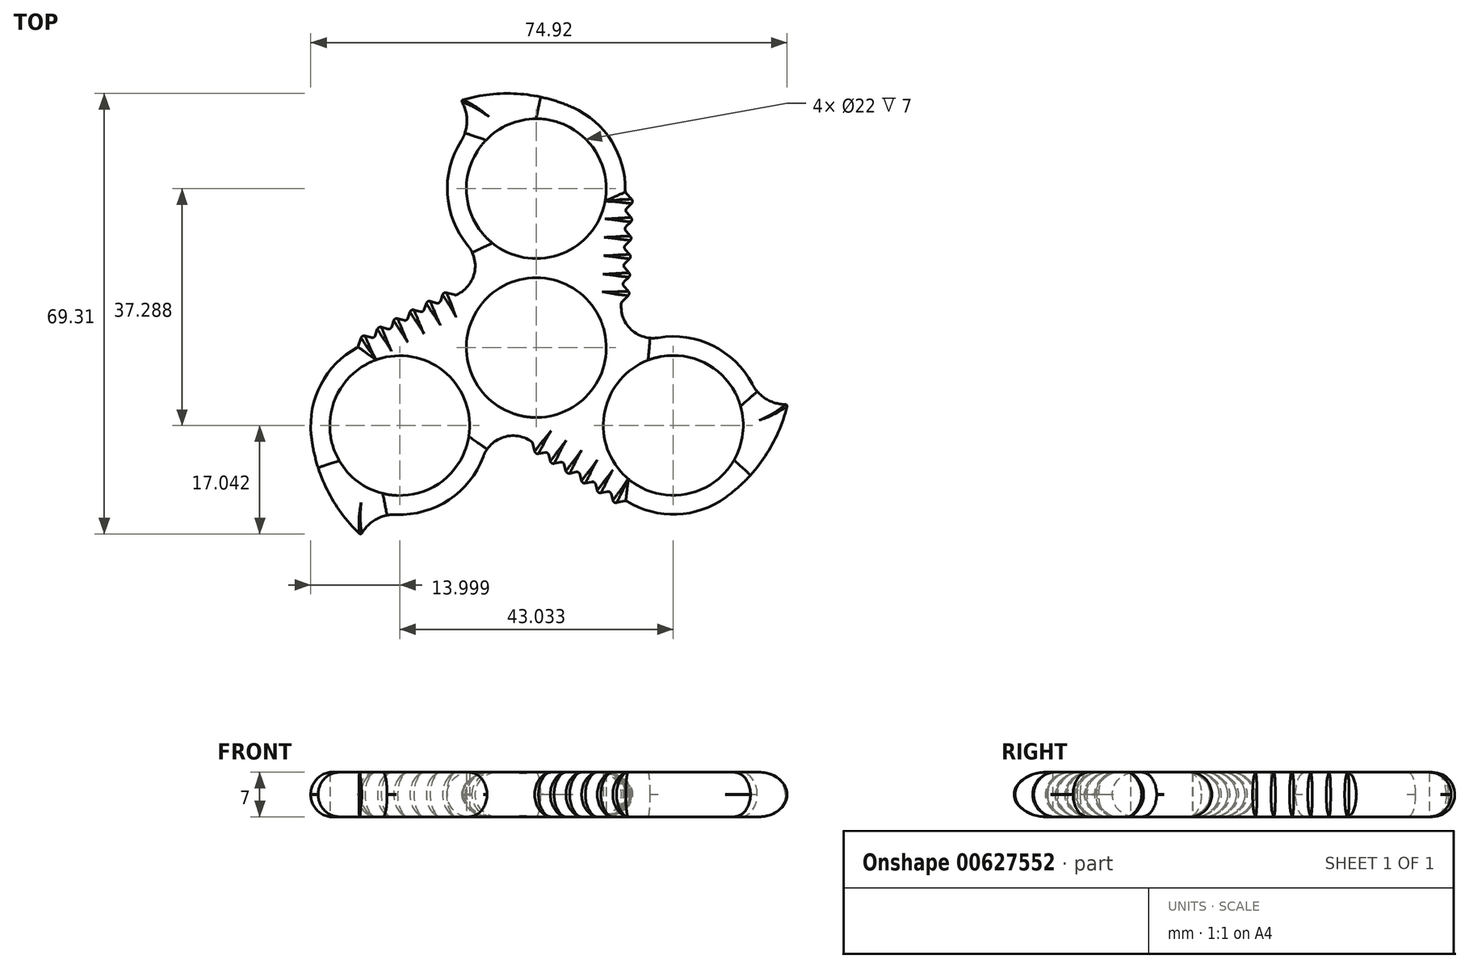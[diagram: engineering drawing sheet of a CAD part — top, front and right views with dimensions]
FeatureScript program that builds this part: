
annotation { "Feature Type Name" : "Feature", "Feature Type Description" : "" }
export const myFeature = defineFeature(function(context is Context, id is Id, definition is map)
    precondition{}
    {
        {
            var Q0;
            Q0=qCreatedBy(makeId("Top.planeOp"),FACE);
            var sketch = newSketch(context, id + "F0", { "sketchPlane" : qUnion([Q0])});
            skCircle(sketch, "E0", {"center": v(0, 0) * mm, "radius": 39 * mm, "construction": true});
            skCircle(sketch, "E1", {"center": v(0, 0) * mm, "radius": 25 * mm, "construction": true});
            skCircle(sketch, "E2", {"center": v(0, 0) * mm, "radius": 11 * mm});
            skCircle(sketch, "E3", {"center": v(0, 25) * mm, "radius": 11 * mm});
            skPoint(sketch, "E4.center", {"position": v(0.03, 0) * mm});
            skArc(sketch, "E5", {"start": v(14, 24.5) * mm, "mid": v(11.9, 32.39) * mm, "end": v(5.75, 37.77) * mm});
            skLineSegment(sketch, "E6", {"start": v(13.35, 6.66) * mm, "end": v(13.36, 7.1) * mm});
            skPoint(sketch, "E7.visualSharp", {"position": v(-4.7, 11.81) * mm});
            skArc(sketch, "E7.filletArc", {"start": v(-12.27, 8.44) * mm, "mid": v(-9.7, 11.89) * mm, "end": v(-10.77, 16.05) * mm});
            skPoint(sketch, "E8.visualSharp", {"position": v(13.05, -1.63) * mm});
            skArc(sketch, "E9", {"start": v(5.75, 37.77) * mm, "mid": v(-2.94, 39.93) * mm, "end": v(-11.83, 38.9) * mm});
            skArc(sketch, "E10", {"start": v(-11.83, 32.48) * mm, "mid": v(-10.9, 35.7) * mm, "end": v(-11.83, 38.9) * mm});
            skArc(sketch, "E11.trimOffspring", {"start": v(-11.83, 32.48) * mm, "mid": v(-13.97, 24.1) * mm, "end": v(-10.77, 16.05) * mm});
            skLineSegment(sketch, "E12", {"start": v(14, 24.5) * mm, "end": v(15.31, 23) * mm});
            skLineSegment(sketch, "E13", {"start": v(15.31, 23) * mm, "end": v(13.89, 21.6) * mm});
            skLineSegment(sketch, "E14.1.0.0", {"start": v(15.2, 20.1) * mm, "end": v(13.78, 18.7) * mm});
            skLineSegment(sketch, "E14.1.0.1", {"start": v(13.89, 21.6) * mm, "end": v(15.2, 20.1) * mm});
            skLineSegment(sketch, "E14.2.0.0", {"start": v(15.1, 17.2) * mm, "end": v(13.68, 15.8) * mm});
            skLineSegment(sketch, "E14.2.0.1", {"start": v(13.78, 18.7) * mm, "end": v(15.1, 17.2) * mm});
            skLineSegment(sketch, "E14.3.0.0", {"start": v(15, 14.3) * mm, "end": v(13.57, 12.9) * mm});
            skLineSegment(sketch, "E14.3.0.1", {"start": v(13.68, 15.8) * mm, "end": v(15, 14.3) * mm});
            skLineSegment(sketch, "E14.4.0.0", {"start": v(14.9, 11.4) * mm, "end": v(13.47, 10) * mm});
            skLineSegment(sketch, "E14.4.0.1", {"start": v(13.57, 12.9) * mm, "end": v(14.9, 11.4) * mm});
            skLineSegment(sketch, "E14.5.0.0", {"start": v(14.79, 8.5) * mm, "end": v(13.36, 7.1) * mm});
            skLineSegment(sketch, "E14.5.0.1", {"start": v(13.47, 10) * mm, "end": v(14.79, 8.5) * mm});
            skArc(sketch, "E15.1.0", {"start": v(-22.04, -26.28) * mm, "mid": v(-25.29, -27.08) * mm, "end": v(-27.6, -29.49) * mm});
            skArc(sketch, "E15.1.1", {"start": v(-1, -14.64) * mm, "mid": v(-5.27, -14.14) * mm, "end": v(-8.35, -17.14) * mm});
            skArc(sketch, "E15.1.2", {"start": v(-22.04, -26.28) * mm, "mid": v(-13.71, -23.93) * mm, "end": v(-8.35, -17.14) * mm});
            skArc(sketch, "E15.1.3", {"start": v(-35.41, -13.7) * mm, "mid": v(-32.94, -22.3) * mm, "end": v(-27.6, -29.49) * mm});
            skArc(sketch, "E15.1.4", {"start": v(-28.04, 0.08) * mm, "mid": v(-33.82, -5.68) * mm, "end": v(-35.41, -13.7) * mm});
            skCircle(sketch, "E15.1.5", {"center": v(-21.48, -12.29) * mm, "radius": 11 * mm});
            skLineSegment(sketch, "E15.1.6", {"start": v(-28.04, 0.08) * mm, "end": v(-27.4, 1.98) * mm});
            skLineSegment(sketch, "E15.1.7", {"start": v(-27.4, 1.98) * mm, "end": v(-25.47, 1.44) * mm});
            skLineSegment(sketch, "E15.1.8", {"start": v(-25.48, 1.44) * mm, "end": v(-24.84, 3.34) * mm});
            skLineSegment(sketch, "E15.1.9", {"start": v(-24.84, 3.34) * mm, "end": v(-22.91, 2.8) * mm});
            skLineSegment(sketch, "E15.1.10", {"start": v(-22.91, 2.8) * mm, "end": v(-22.28, 4.7) * mm});
            skLineSegment(sketch, "E15.1.11", {"start": v(-22.28, 4.7) * mm, "end": v(-20.35, 4.16) * mm});
            skLineSegment(sketch, "E15.1.12", {"start": v(-20.35, 4.16) * mm, "end": v(-19.71, 6.05) * mm});
            skLineSegment(sketch, "E15.1.13", {"start": v(-19.71, 6.05) * mm, "end": v(-17.79, 5.52) * mm});
            skLineSegment(sketch, "E15.1.14", {"start": v(-17.79, 5.51) * mm, "end": v(-17.15, 7.41) * mm});
            skLineSegment(sketch, "E15.1.15", {"start": v(-17.15, 7.41) * mm, "end": v(-15.23, 6.87) * mm});
            skLineSegment(sketch, "E15.1.16", {"start": v(-15.23, 6.87) * mm, "end": v(-14.59, 8.77) * mm});
            skLineSegment(sketch, "E15.1.17", {"start": v(-14.59, 8.77) * mm, "end": v(-12.66, 8.23) * mm});
            skLineSegment(sketch, "E15.1.18", {"start": v(-12.27, 8.44) * mm, "end": v(-12.66, 8.23) * mm});
            skArc(sketch, "E15.2.0", {"start": v(33.95, -5.74) * mm, "mid": v(36.26, -8.15) * mm, "end": v(39.5, -8.95) * mm});
            skArc(sketch, "E15.2.1", {"start": v(13.35, 6.66) * mm, "mid": v(15.05, 2.72) * mm, "end": v(19.19, 1.55) * mm});
            skArc(sketch, "E15.2.2", {"start": v(33.95, -5.74) * mm, "mid": v(27.75, 0.3) * mm, "end": v(19.19, 1.55) * mm});
            skArc(sketch, "E15.2.3", {"start": v(29.73, -23.6) * mm, "mid": v(35.95, -17.16) * mm, "end": v(39.5, -8.95) * mm});
            skArc(sketch, "E15.2.4", {"start": v(14.12, -24.11) * mm, "mid": v(22, -26.24) * mm, "end": v(29.73, -23.6) * mm});
            skCircle(sketch, "E15.2.5", {"center": v(21.55, -12.25) * mm, "radius": 11 * mm});
            skLineSegment(sketch, "E15.2.6", {"start": v(14.12, -24.11) * mm, "end": v(12.16, -24.5) * mm});
            skLineSegment(sketch, "E15.2.7", {"start": v(12.16, -24.5) * mm, "end": v(11.66, -22.57) * mm});
            skLineSegment(sketch, "E15.2.8", {"start": v(11.66, -22.57) * mm, "end": v(9.7, -22.97) * mm});
            skLineSegment(sketch, "E15.2.9", {"start": v(9.7, -22.97) * mm, "end": v(9.2, -21.03) * mm});
            skLineSegment(sketch, "E15.2.10", {"start": v(9.2, -21.03) * mm, "end": v(7.24, -21.43) * mm});
            skLineSegment(sketch, "E15.2.11", {"start": v(7.24, -21.43) * mm, "end": v(6.74, -19.5) * mm});
            skLineSegment(sketch, "E15.2.12", {"start": v(6.75, -19.5) * mm, "end": v(4.79, -19.89) * mm});
            skLineSegment(sketch, "E15.2.13", {"start": v(4.79, -19.89) * mm, "end": v(4.29, -17.95) * mm});
            skLineSegment(sketch, "E15.2.14", {"start": v(4.29, -17.95) * mm, "end": v(2.33, -18.35) * mm});
            skLineSegment(sketch, "E15.2.15", {"start": v(2.33, -18.35) * mm, "end": v(1.83, -16.41) * mm});
            skLineSegment(sketch, "E15.2.16", {"start": v(1.83, -16.41) * mm, "end": v(-0.13, -16.8) * mm});
            skLineSegment(sketch, "E15.2.17", {"start": v(-0.13, -16.8) * mm, "end": v(-0.63, -14.87) * mm});
            skLineSegment(sketch, "E15.2.18", {"start": v(-1, -14.64) * mm, "end": v(-0.63, -14.87) * mm});
            skPoint(sketch, "E15.center", {"position": v(0.02, 0.15) * mm});
            skLineSegment(sketch, "E16.trimOffspring", {"start": v(-25.47, 1.44) * mm, "end": v(-25.48, 1.44) * mm});
            skLineSegment(sketch, "E17.trimOffspring", {"start": v(-22.91, 2.8) * mm, "end": v(-22.91, 2.8) * mm});
            skLineSegment(sketch, "E18.trimOffspring", {"start": v(-20.35, 4.16) * mm, "end": v(-20.35, 4.16) * mm});
            skLineSegment(sketch, "E19.trimOffspring", {"start": v(-17.79, 5.52) * mm, "end": v(-17.79, 5.51) * mm});
            skLineSegment(sketch, "E20.trimOffspring", {"start": v(-15.23, 6.87) * mm, "end": v(-15.23, 6.87) * mm});
            skLineSegment(sketch, "E21.trimOffspring", {"start": v(1.83, -16.41) * mm, "end": v(1.83, -16.41) * mm});
            skLineSegment(sketch, "E22.trimOffspring", {"start": v(4.29, -17.95) * mm, "end": v(4.29, -17.95) * mm});
            skLineSegment(sketch, "E23.trimOffspring", {"start": v(6.74, -19.5) * mm, "end": v(6.75, -19.5) * mm});
            skLineSegment(sketch, "E24.trimOffspring", {"start": v(9.2, -21.03) * mm, "end": v(9.2, -21.03) * mm});
            skLineSegment(sketch, "E25.trimOffspring", {"start": v(11.26, -22.32) * mm, "end": v(11.66, -22.57) * mm});
            skLineSegment(sketch, "E26.trimOffspring", {"start": v(13.47, 10) * mm, "end": v(13.47, 10) * mm});
            skLineSegment(sketch, "E27.trimOffspring", {"start": v(13.57, 12.9) * mm, "end": v(13.57, 12.9) * mm});
            skLineSegment(sketch, "E28.trimOffspring", {"start": v(13.68, 15.8) * mm, "end": v(13.68, 15.8) * mm});
            skLineSegment(sketch, "E29.trimOffspring", {"start": v(13.78, 18.7) * mm, "end": v(13.78, 18.7) * mm});
            skLineSegment(sketch, "E30.trimOffspring", {"start": v(13.78, 18.7) * mm, "end": v(13.78, 18.7) * mm, "construction": true});
            skLineSegment(sketch, "E31.trimOffspring", {"start": v(13.89, 21.6) * mm, "end": v(13.89, 21.6) * mm});
            skSolve(sketch);
        }
        {
            var Q0;
            Q0=qSketchRegion(id+"F0",true);
            extrude(context, id + "F1", {"entities" : qUnion([Q0]), "depth" : 7 * mm, "offsetDistance" : 25 * mm});
        }
        {
            var Q0;
            Q0=makeQuery(id+"F1.opExtrude","SWEPT_EDGE",EDGE,{"disambiguationData":[OSD([sQuery(id+"F0.wireOp",EDGE,"E15.1.17"),sQuery(id+"F0.wireOp",EDGE,"E15.1.18")])]});
            var Q1;
            Q1=makeQuery(id+"F1.opExtrude","SWEPT_EDGE",EDGE,{"disambiguationData":[OSD([sQuery(id+"F0.wireOp",EDGE,"E15.1.16"),sQuery(id+"F0.wireOp",EDGE,"E15.1.17")])]});
            var Q2;
            Q2=makeQuery(id+"F1.opExtrude","SWEPT_EDGE",EDGE,{"disambiguationData":[OSD([sQuery(id+"F0.wireOp",EDGE,"E15.1.15"),sQuery(id+"F0.wireOp",EDGE,"E15.1.16")])]});
            var Q3;
            Q3=makeQuery(id+"F1.opExtrude","SWEPT_EDGE",EDGE,{"disambiguationData":[OSD([sQuery(id+"F0.wireOp",EDGE,"E15.1.14"),sQuery(id+"F0.wireOp",EDGE,"E15.1.15")])]});
            var Q4;
            Q4=makeQuery(id+"F1.opExtrude","SWEPT_EDGE",EDGE,{"disambiguationData":[OSD([sQuery(id+"F0.wireOp",EDGE,"E15.1.13"),sQuery(id+"F0.wireOp",EDGE,"E15.1.14")])]});
            var Q5;
            Q5=makeQuery(id+"F1.opExtrude","SWEPT_EDGE",EDGE,{"disambiguationData":[OSD([sQuery(id+"F0.wireOp",EDGE,"E15.1.12"),sQuery(id+"F0.wireOp",EDGE,"E15.1.13")])]});
            var Q6;
            Q6=makeQuery(id+"F1.opExtrude","SWEPT_EDGE",EDGE,{"disambiguationData":[OSD([sQuery(id+"F0.wireOp",EDGE,"E15.1.11"),sQuery(id+"F0.wireOp",EDGE,"E15.1.12")])]});
            var Q7;
            Q7=makeQuery(id+"F1.opExtrude","SWEPT_EDGE",EDGE,{"disambiguationData":[OSD([sQuery(id+"F0.wireOp",EDGE,"E15.1.10"),sQuery(id+"F0.wireOp",EDGE,"E15.1.11")])]});
            var Q8;
            Q8=makeQuery(id+"F1.opExtrude","SWEPT_EDGE",EDGE,{"disambiguationData":[OSD([sQuery(id+"F0.wireOp",EDGE,"E15.1.9"),sQuery(id+"F0.wireOp",EDGE,"E15.1.10")])]});
            var Q9;
            Q9=makeQuery(id+"F1.opExtrude","SWEPT_EDGE",EDGE,{"disambiguationData":[OSD([sQuery(id+"F0.wireOp",EDGE,"E15.1.8"),sQuery(id+"F0.wireOp",EDGE,"E15.1.9")])]});
            var Q10;
            Q10=makeQuery(id+"F1.opExtrude","SWEPT_EDGE",EDGE,{"disambiguationData":[OSD([sQuery(id+"F0.wireOp",EDGE,"E15.1.7"),sQuery(id+"F0.wireOp",EDGE,"E15.1.8")])]});
            var Q11;
            Q11=makeQuery(id+"F1.opExtrude","SWEPT_EDGE",EDGE,{"disambiguationData":[OSD([sQuery(id+"F0.wireOp",EDGE,"E15.1.6"),sQuery(id+"F0.wireOp",EDGE,"E15.1.7")])]});
            var Q12;
            Q12=makeQuery(id+"F1.opExtrude","SWEPT_EDGE",EDGE,{"disambiguationData":[OSD([sQuery(id+"F0.wireOp",EDGE,"E15.1.4"),sQuery(id+"F0.wireOp",EDGE,"E15.1.6")])]});
            var Q13;
            Q13=makeQuery(id+"F1.opExtrude","SWEPT_EDGE",EDGE,{"disambiguationData":[OSD([sQuery(id+"F0.wireOp",EDGE,"E15.2.17"),sQuery(id+"F0.wireOp",EDGE,"E15.2.18")])]});
            var Q14;
            Q14=makeQuery(id+"F1.opExtrude","SWEPT_EDGE",EDGE,{"disambiguationData":[OSD([sQuery(id+"F0.wireOp",EDGE,"E15.2.16"),sQuery(id+"F0.wireOp",EDGE,"E15.2.17")])]});
            var Q15;
            Q15=makeQuery(id+"F1.opExtrude","SWEPT_EDGE",EDGE,{"disambiguationData":[OSD([sQuery(id+"F0.wireOp",EDGE,"E15.2.15"),sQuery(id+"F0.wireOp",EDGE,"E15.2.16")])]});
            var Q16;
            Q16=makeQuery(id+"F1.opExtrude","SWEPT_EDGE",EDGE,{"disambiguationData":[OSD([sQuery(id+"F0.wireOp",EDGE,"E15.2.14"),sQuery(id+"F0.wireOp",EDGE,"E15.2.15")])]});
            var Q17;
            Q17=makeQuery(id+"F1.opExtrude","SWEPT_EDGE",EDGE,{"disambiguationData":[OSD([sQuery(id+"F0.wireOp",EDGE,"E15.2.13"),sQuery(id+"F0.wireOp",EDGE,"E15.2.14")])]});
            var Q18;
            Q18=makeQuery(id+"F1.opExtrude","SWEPT_EDGE",EDGE,{"disambiguationData":[OSD([sQuery(id+"F0.wireOp",EDGE,"E15.2.12"),sQuery(id+"F0.wireOp",EDGE,"E15.2.13")])]});
            var Q19;
            Q19=makeQuery(id+"F1.opExtrude","SWEPT_EDGE",EDGE,{"disambiguationData":[OSD([sQuery(id+"F0.wireOp",EDGE,"E15.2.11"),sQuery(id+"F0.wireOp",EDGE,"E15.2.12")])]});
            var Q20;
            Q20=makeQuery(id+"F1.opExtrude","SWEPT_EDGE",EDGE,{"disambiguationData":[OSD([sQuery(id+"F0.wireOp",EDGE,"E15.2.10"),sQuery(id+"F0.wireOp",EDGE,"E15.2.11")])]});
            var Q21;
            Q21=makeQuery(id+"F1.opExtrude","SWEPT_EDGE",EDGE,{"disambiguationData":[OSD([sQuery(id+"F0.wireOp",EDGE,"E15.2.9"),sQuery(id+"F0.wireOp",EDGE,"E15.2.10")])]});
            var Q22;
            Q22=makeQuery(id+"F1.opExtrude","SWEPT_EDGE",EDGE,{"disambiguationData":[OSD([sQuery(id+"F0.wireOp",EDGE,"E15.2.8"),sQuery(id+"F0.wireOp",EDGE,"E15.2.9")])]});
            var Q23;
            Q23=makeQuery(id+"F1.opExtrude","SWEPT_EDGE",EDGE,{"disambiguationData":[OSD([sQuery(id+"F0.wireOp",EDGE,"E15.2.7"),sQuery(id+"F0.wireOp",EDGE,"E15.2.8")])]});
            var Q24;
            Q24=makeQuery(id+"F1.opExtrude","SWEPT_EDGE",EDGE,{"disambiguationData":[OSD([sQuery(id+"F0.wireOp",EDGE,"E15.2.6"),sQuery(id+"F0.wireOp",EDGE,"E15.2.7")])]});
            var Q25;
            Q25=makeQuery(id+"F1.opExtrude","SWEPT_EDGE",EDGE,{"disambiguationData":[OSD([sQuery(id+"F0.wireOp",EDGE,"E15.2.4"),sQuery(id+"F0.wireOp",EDGE,"E15.2.6")])]});
            var Q26;
            Q26=makeQuery(id+"F1.opExtrude","SWEPT_EDGE",EDGE,{"disambiguationData":[OSD([sQuery(id+"F0.wireOp",EDGE,"E5"),sQuery(id+"F0.wireOp",EDGE,"E12")])]});
            var Q27;
            Q27=makeQuery(id+"F1.opExtrude","SWEPT_EDGE",EDGE,{"disambiguationData":[OSD([sQuery(id+"F0.wireOp",EDGE,"E12"),sQuery(id+"F0.wireOp",EDGE,"E13")])]});
            var Q28;
            Q28=makeQuery(id+"F1.opExtrude","SWEPT_EDGE",EDGE,{"disambiguationData":[OSD([sQuery(id+"F0.wireOp",EDGE,"E13"),sQuery(id+"F0.wireOp",EDGE,"E14.1.0.1")])]});
            var Q29;
            Q29=makeQuery(id+"F1.opExtrude","SWEPT_EDGE",EDGE,{"disambiguationData":[OSD([sQuery(id+"F0.wireOp",EDGE,"E14.1.0.0"),sQuery(id+"F0.wireOp",EDGE,"E14.1.0.1")])]});
            var Q30;
            Q30=makeQuery(id+"F1.opExtrude","SWEPT_EDGE",EDGE,{"disambiguationData":[OSD([sQuery(id+"F0.wireOp",EDGE,"E14.1.0.0"),sQuery(id+"F0.wireOp",EDGE,"E14.2.0.1")])]});
            var Q31;
            Q31=makeQuery(id+"F1.opExtrude","SWEPT_EDGE",EDGE,{"disambiguationData":[OSD([sQuery(id+"F0.wireOp",EDGE,"E14.2.0.0"),sQuery(id+"F0.wireOp",EDGE,"E14.2.0.1")])]});
            var Q32;
            Q32=makeQuery(id+"F1.opExtrude","SWEPT_EDGE",EDGE,{"disambiguationData":[OSD([sQuery(id+"F0.wireOp",EDGE,"E14.2.0.0"),sQuery(id+"F0.wireOp",EDGE,"E14.3.0.1")])]});
            var Q33;
            Q33=makeQuery(id+"F1.opExtrude","SWEPT_EDGE",EDGE,{"disambiguationData":[OSD([sQuery(id+"F0.wireOp",EDGE,"E14.3.0.0"),sQuery(id+"F0.wireOp",EDGE,"E14.3.0.1")])]});
            var Q34;
            Q34=makeQuery(id+"F1.opExtrude","SWEPT_EDGE",EDGE,{"disambiguationData":[OSD([sQuery(id+"F0.wireOp",EDGE,"E14.3.0.0"),sQuery(id+"F0.wireOp",EDGE,"E14.4.0.1")])]});
            var Q35;
            Q35=makeQuery(id+"F1.opExtrude","SWEPT_EDGE",EDGE,{"disambiguationData":[OSD([sQuery(id+"F0.wireOp",EDGE,"E14.4.0.0"),sQuery(id+"F0.wireOp",EDGE,"E14.4.0.1")])]});
            var Q36;
            Q36=makeQuery(id+"F1.opExtrude","SWEPT_EDGE",EDGE,{"disambiguationData":[OSD([sQuery(id+"F0.wireOp",EDGE,"E14.4.0.0"),sQuery(id+"F0.wireOp",EDGE,"E14.5.0.1")])]});
            var Q37;
            Q37=makeQuery(id+"F1.opExtrude","SWEPT_EDGE",EDGE,{"disambiguationData":[OSD([sQuery(id+"F0.wireOp",EDGE,"E14.5.0.0"),sQuery(id+"F0.wireOp",EDGE,"E14.5.0.1")])]});
            var Q38;
            Q38=makeQuery(id+"F1.opExtrude","SWEPT_EDGE",EDGE,{"disambiguationData":[OSD([sQuery(id+"F0.wireOp",EDGE,"E6"),sQuery(id+"F0.wireOp",EDGE,"E14.5.0.0")])]});
            fillet(context, id + "F2", {"entities" : qUnion([Q0, Q1, Q2, Q3, Q4, Q5, Q6, Q7, Q8, Q9, Q10, Q11, Q12, Q13, Q14, Q15, Q16, Q17, Q18, Q19, Q20, Q21, Q22, Q23, Q24, Q25, Q26, Q27, Q28, Q29, Q30, Q31, Q32, Q33, Q34, Q35, Q36, Q37, Q38]), "radius" : .5 * mm, "tangentPropagation" : true, "allowEdgeOverflow" : false});
        }
        {
            var Q0;
            Q0=makeQuery(id+"F1.opExtrude","SWEPT_EDGE",EDGE,{"disambiguationData":[OSD([sQuery(id+"F0.wireOp",EDGE,"E9"),sQuery(id+"F0.wireOp",EDGE,"E10")])]});
            var Q1;
            Q1=makeQuery(id+"F1.opExtrude","SWEPT_EDGE",EDGE,{"disambiguationData":[OSD([sQuery(id+"F0.wireOp",EDGE,"E15.1.0"),sQuery(id+"F0.wireOp",EDGE,"E15.1.3")])]});
            var Q2;
            Q2=makeQuery(id+"F1.opExtrude","SWEPT_EDGE",EDGE,{"disambiguationData":[OSD([sQuery(id+"F0.wireOp",EDGE,"E15.2.0"),sQuery(id+"F0.wireOp",EDGE,"E15.2.3")])]});
            fillet(context, id + "F3", {"entities" : qUnion([Q0, Q1, Q2]), "radius" : .25 * mm, "tangentPropagation" : true, "allowEdgeOverflow" : false});
        }
        {
            var Q0;
            Q0=makeQuery(id+"F1.opExtrude","CAP_EDGE",EDGE,{"disambiguationData":[OSD([sQuery(id+"F0.wireOp",EDGE,"E15.2.4")])],"isStart":false});
            var Q1;
            Q1=makeQuery(id+"F1.opExtrude","CAP_EDGE",EDGE,{"disambiguationData":[OSD([sQuery(id+"F0.wireOp",EDGE,"E15.1.1")])],"isStart":true});
            fillet(context, id + "F4", {"entities" : qUnion([Q0, Q1]), "radius" : 3.5 * mm, "tangentPropagation" : true, "allowEdgeOverflow" : false});
        }
    });
